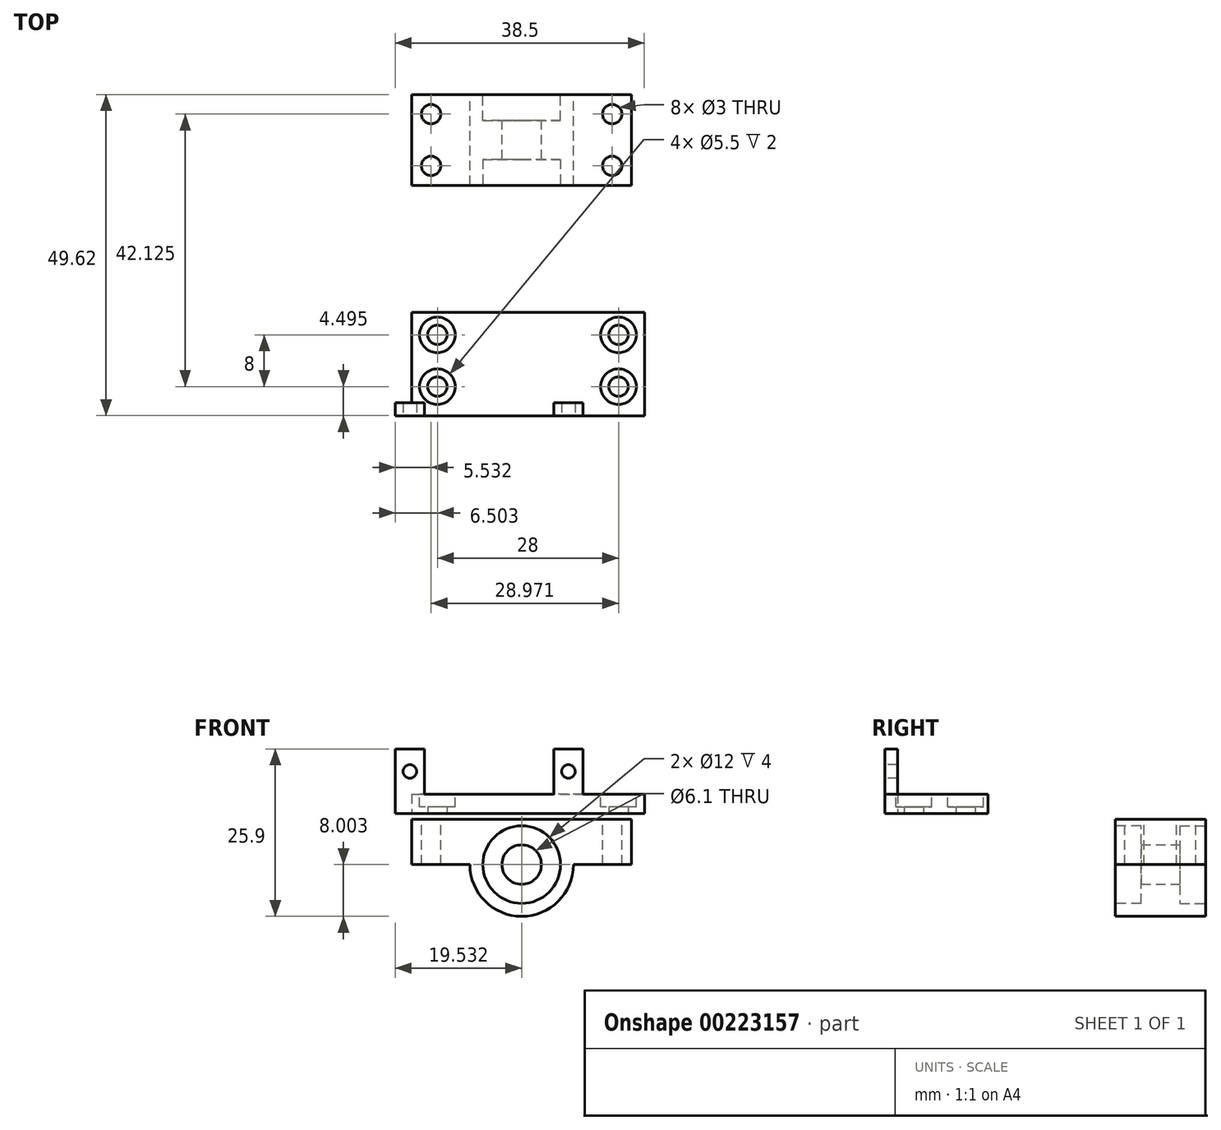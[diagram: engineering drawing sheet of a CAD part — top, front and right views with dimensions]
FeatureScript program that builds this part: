
annotation { "Feature Type Name" : "Feature", "Feature Type Description" : "" }
export const myFeature = defineFeature(function(context is Context, id is Id, definition is map)
    precondition{}
    {
        {
            var Q0;
            Q0=qCreatedBy(makeId("Front.planeOp"),FACE);
            var sketch = newSketch(context, id + "F0", { "sketchPlane" : qUnion([Q0])});
            skArc(sketch, "E0", {"start": v(-56.83, -7.9) * mm, "mid": v(-48.83, -15.9) * mm, "end": v(-40.83, -7.9) * mm});
            skCircle(sketch, "E1", {"center": v(-48.83, -7.9) * mm, "radius": 3.05 * mm});
            skLineSegment(sketch, "E2", {"start": v(-40.83, -7.9) * mm, "end": v(-31.83, -7.9) * mm});
            skLineSegment(sketch, "E3", {"start": v(-31.83, -7.9) * mm, "end": v(-31.83, -0.9) * mm});
            skLineSegment(sketch, "E4", {"start": v(-31.83, -0.9) * mm, "end": v(-65.83, -0.9) * mm});
            skLineSegment(sketch, "E5", {"start": v(-65.83, -0.9) * mm, "end": v(-65.83, -7.9) * mm});
            skLineSegment(sketch, "E6", {"start": v(-65.83, -7.9) * mm, "end": v(-56.83, -7.9) * mm});
            skSolve(sketch);
        }
        {
            var Q0;
            Q0 = qSketchRegion(id + "F0", true);
            extrude(context, id + "F1", {"entities" : qUnion([Q0]), "depth" : 14 * mm});
        }
        {
            var Q0;
            Q0=makeQuery(id+"F1.opExtrude","CAP_FACE",FACE,{"disambiguationData":[OSD([sQuery(id+"F0.wireOp",EDGE,"E0"),sQuery(id+"F0.wireOp",EDGE,"E1"),sQuery(id+"F0.wireOp",EDGE,"E2"),sQuery(id+"F0.wireOp",EDGE,"E3"),sQuery(id+"F0.wireOp",EDGE,"E4"),sQuery(id+"F0.wireOp",EDGE,"E5"),sQuery(id+"F0.wireOp",EDGE,"E6")])],"isStart":false});
            var sketch = newSketch(context, id + "F2", { "sketchPlane" : qUnion([Q0])});
            skCircle(sketch, "E7", {"center": v(-48.83, -7.9) * mm, "radius": 6 * mm});
            skSolve(sketch);
        }
        {
            var Q0;
            Q0 = qSketchRegion(id + "F2", true);
            extrude(context, id + "F3", {"entities" : qUnion([Q0]), "operationType" : NewBodyOperationType.REMOVE, "oppositeDirection" : true, "depth" : 4 * mm});
        }
        {
            var Q0;
            Q0=makeQuery(id+"F1.opExtrude","CAP_FACE",FACE,{"disambiguationData":[OSD([sQuery(id+"F0.wireOp",EDGE,"E0"),sQuery(id+"F0.wireOp",EDGE,"E1"),sQuery(id+"F0.wireOp",EDGE,"E2"),sQuery(id+"F0.wireOp",EDGE,"E3"),sQuery(id+"F0.wireOp",EDGE,"E4"),sQuery(id+"F0.wireOp",EDGE,"E5"),sQuery(id+"F0.wireOp",EDGE,"E6")])],"isStart":true});
            var sketch = newSketch(context, id + "F4", { "sketchPlane" : qUnion([Q0])});
            skCircle(sketch, "E8", {"center": v(48.83, -7.9) * mm, "radius": 6 * mm});
            skSolve(sketch);
        }
        {
            var Q0;
            Q0 = qSketchRegion(id + "F4", true);
            extrude(context, id + "F5", {"entities" : qUnion([Q0]), "operationType" : NewBodyOperationType.REMOVE, "oppositeDirection" : true, "depth" : 4 * mm});
        }
        {
            var Q0;
            Q0=makeQuery(id+"F1.opExtrude","SWEPT_FACE",FACE,{"disambiguationData":[OSD([sQuery(id+"F0.wireOp",EDGE,"E4")])]});
            var sketch = newSketch(context, id + "F6", { "sketchPlane" : qUnion([Q0])});
            skCircle(sketch, "E9", {"center": v(-62.83, -3) * mm, "radius": 1.5 * mm});
            skCircle(sketch, "E10", {"center": v(-34.83, -3) * mm, "radius": 1.5 * mm});
            skCircle(sketch, "E11", {"center": v(-34.83, -11) * mm, "radius": 1.5 * mm});
            skCircle(sketch, "E12", {"center": v(-62.83, -11) * mm, "radius": 1.5 * mm});
            skSolve(sketch);
        }
        {
            var Q0;
            Q0 = qSketchRegion(id + "F6", true);
            extrude(context, id + "F7", {"entities" : qUnion([Q0]), "operationType" : NewBodyOperationType.REMOVE, "endBound" : BoundingType.THROUGH_ALL, "oppositeDirection" : true, "depth" : 25 * mm});
        }
        {
            var Q0;
            Q0=qCreatedBy(makeId("Top.planeOp"),FACE);
            var sketch = newSketch(context, id + "F8", { "sketchPlane" : qUnion([Q0])});
            skLineSegment(sketch, "E13.bottom", {"start": v(-65.86, -33.62) * mm, "end": v(-29.86, -33.62) * mm});
            skLineSegment(sketch, "E13.top", {"start": v(-65.86, -49.62) * mm, "end": v(-29.86, -49.62) * mm});
            skLineSegment(sketch, "E13.left", {"start": v(-65.86, -33.62) * mm, "end": v(-65.86, -49.62) * mm});
            skLineSegment(sketch, "E13.right", {"start": v(-29.86, -33.62) * mm, "end": v(-29.86, -49.62) * mm});
            skCircle(sketch, "E14", {"center": v(-61.86, -37.12) * mm, "radius": 1.5 * mm});
            skCircle(sketch, "E15", {"center": v(-33.86, -37.12) * mm, "radius": 1.5 * mm});
            skCircle(sketch, "E16", {"center": v(-33.86, -45.12) * mm, "radius": 1.5 * mm});
            skCircle(sketch, "E17", {"center": v(-61.86, -45.12) * mm, "radius": 1.5 * mm});
            skSolve(sketch);
        }
        {
            var Q0;
            Q0 = qSketchRegion(id + "F8", true);
            extrude(context, id + "F9", {"entities" : qUnion([Q0]), "depth" : 3 * mm});
        }
        {
            var Q0;
            Q0=makeQuery(id+"F9.opExtrude","CAP_FACE",FACE,{"disambiguationData":[OSD([sQuery(id+"F8.wireOp",EDGE,"E13.bottom"),sQuery(id+"F8.wireOp",EDGE,"E13.top"),sQuery(id+"F8.wireOp",EDGE,"E13.left"),sQuery(id+"F8.wireOp",EDGE,"E13.right"),sQuery(id+"F8.wireOp",EDGE,"E14"),sQuery(id+"F8.wireOp",EDGE,"E15"),sQuery(id+"F8.wireOp",EDGE,"E16"),sQuery(id+"F8.wireOp",EDGE,"E17")])],"isStart":false});
            var sketch = newSketch(context, id + "F10", { "sketchPlane" : qUnion([Q0])});
            skCircle(sketch, "E18", {"center": v(-61.86, -37.12) * mm, "radius": 2.75 * mm});
            skCircle(sketch, "E19", {"center": v(-33.86, -37.12) * mm, "radius": 2.75 * mm});
            skCircle(sketch, "E20", {"center": v(-61.86, -45.12) * mm, "radius": 2.75 * mm});
            skCircle(sketch, "E21", {"center": v(-33.86, -45.12) * mm, "radius": 2.75 * mm});
            skSolve(sketch);
        }
        {
            var Q0;
            Q0 = qSketchRegion(id + "F10", true);
            extrude(context, id + "F11", {"entities" : qUnion([Q0]), "operationType" : NewBodyOperationType.REMOVE, "oppositeDirection" : true, "depth" : 2 * mm});
        }
        {
            var Q0;
            Q0=makeQuery(id+"F9.opExtrude","CAP_FACE",FACE,{"disambiguationData":[OSD([sQuery(id+"F8.wireOp",EDGE,"E13.bottom"),sQuery(id+"F8.wireOp",EDGE,"E13.top"),sQuery(id+"F8.wireOp",EDGE,"E13.left"),sQuery(id+"F8.wireOp",EDGE,"E13.right"),sQuery(id+"F8.wireOp",EDGE,"E14"),sQuery(id+"F8.wireOp",EDGE,"E15"),sQuery(id+"F8.wireOp",EDGE,"E16"),sQuery(id+"F8.wireOp",EDGE,"E17")])],"isStart":false});
            var sketch = newSketch(context, id + "F12", { "sketchPlane" : qUnion([Q0])});
            skLineSegment(sketch, "E22.bottom", {"start": v(-43.86, -49.62) * mm, "end": v(-39.36, -49.62) * mm});
            skLineSegment(sketch, "E22.top", {"start": v(-43.86, -47.62) * mm, "end": v(-39.36, -47.62) * mm});
            skLineSegment(sketch, "E22.left", {"start": v(-43.86, -49.62) * mm, "end": v(-43.86, -47.62) * mm});
            skLineSegment(sketch, "E22.right", {"start": v(-39.36, -49.62) * mm, "end": v(-39.36, -47.62) * mm});
            skLineSegment(sketch, "E23.bottom", {"start": v(-63.86, -49.62) * mm, "end": v(-68.36, -49.62) * mm});
            skLineSegment(sketch, "E23.top", {"start": v(-63.86, -47.62) * mm, "end": v(-68.36, -47.62) * mm});
            skLineSegment(sketch, "E23.left", {"start": v(-63.86, -49.62) * mm, "end": v(-63.86, -47.62) * mm});
            skLineSegment(sketch, "E23.right", {"start": v(-68.36, -49.62) * mm, "end": v(-68.36, -47.62) * mm});
            skSolve(sketch);
        }
        {
            var Q0;
            Q0 = qSketchRegion(id + "F12", true);
            extrude(context, id + "F13", {"entities" : qUnion([Q0]), "operationType" : NewBodyOperationType.ADD, "depth" : 7 * mm, "hasSecondDirection" : true, "secondDirectionOppositeDirection" : true, "secondDirectionDepth" : 3 * mm});
        }
        {
            var Q0;
            Q0=makeQuery(id+"F13.boolean.opBoolean","MERGE",FACE,{"derivedFrom":[makeQuery(id+"F9.opExtrude","SWEPT_FACE",FACE,{"disambiguationData":[OSD([sQuery(id+"F8.wireOp",EDGE,"E13.top")])]}),makeQuery(id+"F13.opExtrude","SWEPT_FACE",FACE,{"disambiguationData":[OSD([sQuery(id+"F12.wireOp",EDGE,"E22.bottom")])]}),makeQuery(id+"F13.opExtrude","SWEPT_FACE",FACE,{"disambiguationData":[OSD([sQuery(id+"F12.wireOp",EDGE,"E23.bottom")])]})]});
            var sketch = newSketch(context, id + "F14", { "sketchPlane" : qUnion([Q0])});
            skCircle(sketch, "E24", {"center": v(-41.6, 6.5) * mm, "radius": 1.05 * mm});
            skPoint(sketch, "E24.centerSnap0", {"position": v(-41.6, 10) * mm});
            skPoint(sketch, "E24.centerSnap1", {"position": v(-43.86, 6.5) * mm});
            skCircle(sketch, "E25", {"center": v(-66.1, 6.5) * mm, "radius": 1.05 * mm});
            skPoint(sketch, "E25.centerSnap0", {"position": v(-63.86, 6.5) * mm});
            skPoint(sketch, "E25.centerSnap1", {"position": v(-66.1, 10) * mm});
            skSolve(sketch);
        }
        {
            var Q0;
            Q0 = qSketchRegion(id + "F14", true);
            extrude(context, id + "F15", {"entities" : qUnion([Q0]), "operationType" : NewBodyOperationType.REMOVE, "endBound" : BoundingType.THROUGH_ALL, "oppositeDirection" : true, "depth" : 25 * mm});
        }
    });
